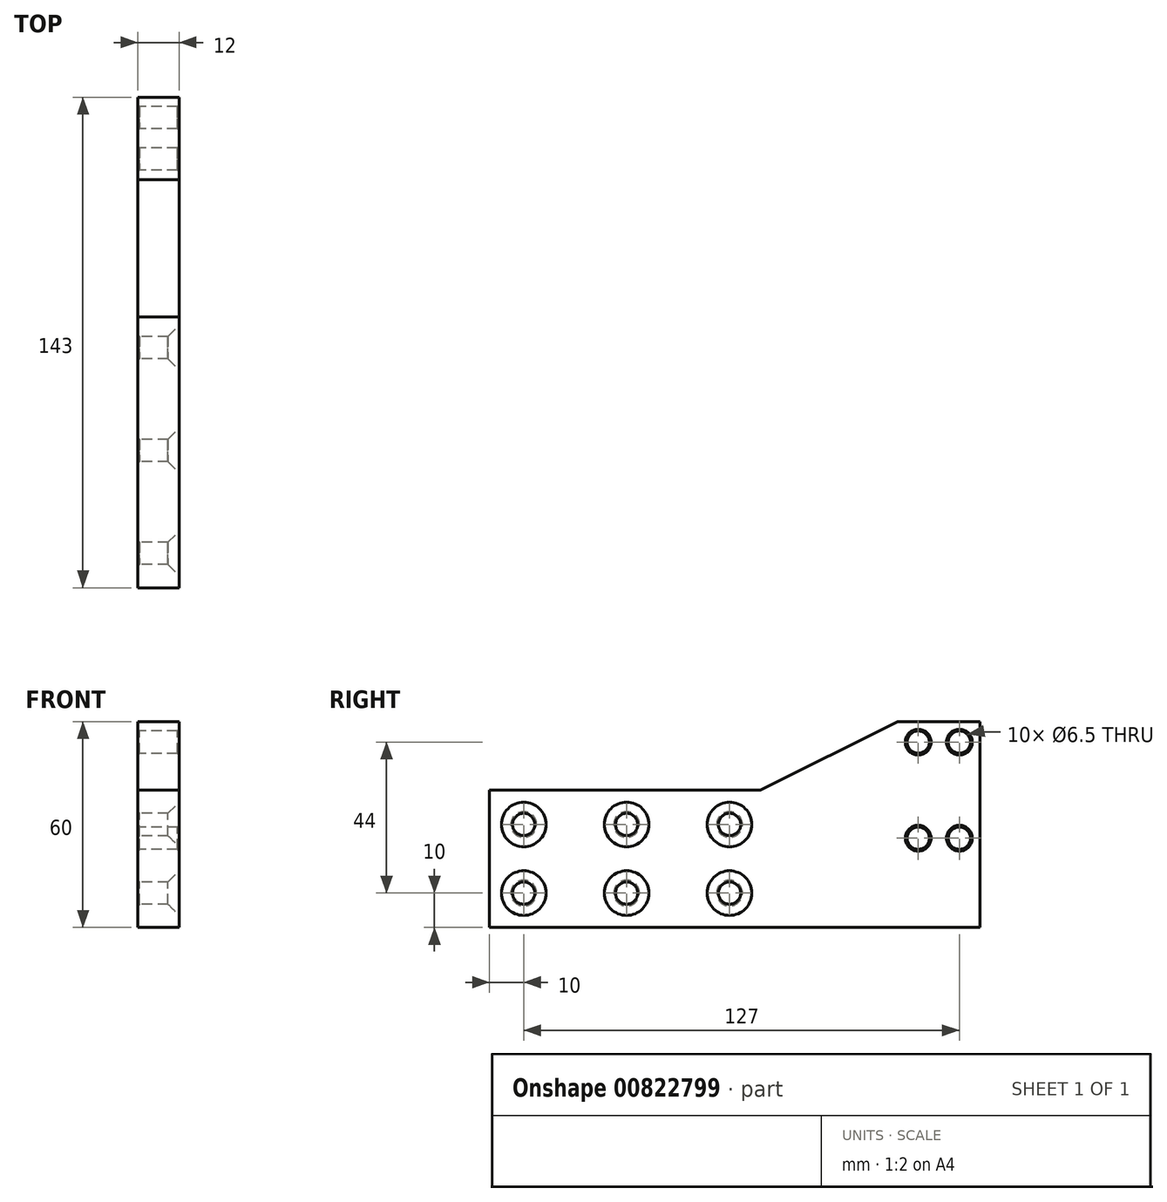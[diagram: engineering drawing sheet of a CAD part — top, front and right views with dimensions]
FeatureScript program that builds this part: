
annotation { "Feature Type Name" : "Feature", "Feature Type Description" : "" }
export const myFeature = defineFeature(function(context is Context, id is Id, definition is map)
    precondition{}
    {
        {
            var Q0;
            Q0=qCreatedBy(makeId("Right.planeOp"),FACE);
            var sketch = newSketch(context, id + "F0", { "sketchPlane" : qUnion([Q0])});
            skLineSegment(sketch, "E0.bottom", {"start": v(-71.5, 20) * mm, "end": v(7.5, 20) * mm});
            skLineSegment(sketch, "E0.top", {"start": v(-71.5, -20) * mm, "end": v(71.5, -20) * mm});
            skLineSegment(sketch, "E0.left", {"start": v(-71.5, 20) * mm, "end": v(-71.5, -20) * mm});
            skLineSegment(sketch, "E0.right", {"start": v(71.5, 20) * mm, "end": v(71.5, -20) * mm});
            skPoint(sketch, "E0.middle", {"position": v(0, 0) * mm});
            skCircle(sketch, "E1", {"center": v(-61.5, 10) * mm, "radius": 3.25 * mm});
            skLineSegment(sketch, "E2", {"start": v(-61.5, 10) * mm, "end": v(-1.5, 10) * mm, "construction": true});
            skCircle(sketch, "E3", {"center": v(-1.5, 10) * mm, "radius": 3.25 * mm});
            skCircle(sketch, "E4", {"center": v(-31.5, 10) * mm, "radius": 3.25 * mm});
            skLineSegment(sketch, "E5", {"start": v(0, 0) * mm, "end": v(-27.42, 0) * mm, "construction": true});
            skCircle(sketch, "E6.MirrorC", {"center": v(-1.5, -10) * mm, "radius": 3.25 * mm});
            skCircle(sketch, "E7.MirrorC", {"center": v(-31.5, -10) * mm, "radius": 3.25 * mm});
            skCircle(sketch, "E8.MirrorC", {"center": v(-61.5, -10) * mm, "radius": 3.25 * mm});
            skLineSegment(sketch, "E9.3", {"start": v(65.5, 34) * mm, "end": v(65.5, 6) * mm, "construction": true});
            skLineSegment(sketch, "E10", {"start": v(47.5, 20) * mm, "end": v(47.5, -20) * mm, "construction": true});
            skCircle(sketch, "E11", {"center": v(65.5, 34) * mm, "radius": 3.25 * mm});
            skCircle(sketch, "E12", {"center": v(53.5, 34) * mm, "radius": 3.25 * mm});
            skCircle(sketch, "E13", {"center": v(53.5, 6) * mm, "radius": 3.25 * mm});
            skCircle(sketch, "E14", {"center": v(65.5, 6) * mm, "radius": 3.25 * mm});
            skLineSegment(sketch, "E15", {"start": v(71.5, 20) * mm, "end": v(71.5, 40) * mm});
            skLineSegment(sketch, "E16", {"start": v(71.5, 40) * mm, "end": v(47.5, 40) * mm});
            skLineSegment(sketch, "E17", {"start": v(47.5, 40) * mm, "end": v(7.5, 20) * mm});
            skLineSegment(sketch, "E18", {"start": v(65.5, 6) * mm, "end": v(53.5, 6) * mm, "construction": true});
            skLineSegment(sketch, "E19", {"start": v(65.5, 34) * mm, "end": v(53.5, 34) * mm, "construction": true});
            skLineSegment(sketch, "E20", {"start": v(53.5, 6) * mm, "end": v(53.5, 34) * mm, "construction": true});
            skSolve(sketch);
        }
        {
            var Q0;
            Q0 = qSketchRegion(id + "F0", true);
            extrude(context, id + "F1", {"entities" : qUnion([Q0]), "depth" : 12 * mm, "offsetDistance" : 25 * mm});
        }
        {
            var Q0;
            Q0=makeQuery(id+"F1.opExtrude","CAP_EDGE",EDGE,{"disambiguationData":[OSD([sQuery(id+"F0.wireOp",EDGE,"E1")])],"isStart":false});
            var Q1;
            Q1=makeQuery(id+"F1.opExtrude","CAP_EDGE",EDGE,{"disambiguationData":[OSD([sQuery(id+"F0.wireOp",EDGE,"E4")])],"isStart":false});
            var Q2;
            Q2=makeQuery(id+"F1.opExtrude","CAP_EDGE",EDGE,{"disambiguationData":[OSD([sQuery(id+"F0.wireOp",EDGE,"E3")])],"isStart":false});
            var Q3;
            Q3=makeQuery(id+"F1.opExtrude","CAP_EDGE",EDGE,{"disambiguationData":[OSD([sQuery(id+"F0.wireOp",EDGE,"E6.MirrorC")])],"isStart":false});
            var Q4;
            Q4=makeQuery(id+"F1.opExtrude","CAP_EDGE",EDGE,{"disambiguationData":[OSD([sQuery(id+"F0.wireOp",EDGE,"E7.MirrorC")])],"isStart":false});
            var Q5;
            Q5=makeQuery(id+"F1.opExtrude","CAP_EDGE",EDGE,{"disambiguationData":[OSD([sQuery(id+"F0.wireOp",EDGE,"E8.MirrorC")])],"isStart":false});
            chamfer(context, id + "F2", {"entities" : qUnion([Q0, Q1, Q2, Q3, Q4, Q5]), "width" : 3.25 * mm, "tangentPropagation" : true});
        }
        {
            var Q0;
            Q0=makeQuery(id+"F1.opExtrude","CAP_EDGE",EDGE,{"disambiguationData":[OSD([sQuery(id+"F0.wireOp",EDGE,"E6.MirrorC")])],"isStart":true});
            var Q1;
            Q1=makeQuery(id+"F1.opExtrude","CAP_EDGE",EDGE,{"disambiguationData":[OSD([sQuery(id+"F0.wireOp",EDGE,"E3")])],"isStart":true});
            var Q2;
            Q2=makeQuery(id+"F1.opExtrude","CAP_EDGE",EDGE,{"disambiguationData":[OSD([sQuery(id+"F0.wireOp",EDGE,"E4")])],"isStart":true});
            var Q3;
            Q3=makeQuery(id+"F1.opExtrude","CAP_EDGE",EDGE,{"disambiguationData":[OSD([sQuery(id+"F0.wireOp",EDGE,"E7.MirrorC")])],"isStart":true});
            var Q4;
            Q4=makeQuery(id+"F1.opExtrude","CAP_EDGE",EDGE,{"disambiguationData":[OSD([sQuery(id+"F0.wireOp",EDGE,"E8.MirrorC")])],"isStart":true});
            var Q5;
            Q5=makeQuery(id+"F1.opExtrude","CAP_EDGE",EDGE,{"disambiguationData":[OSD([sQuery(id+"F0.wireOp",EDGE,"E1")])],"isStart":true});
            var Q6;
            Q6=makeQuery(id+"F1.opExtrude","SWEPT_FACE",FACE,{"disambiguationData":[OSD([sQuery(id+"F0.wireOp",EDGE,"E11")])]});
            var Q7;
            Q7=makeQuery(id+"F1.opExtrude","SWEPT_FACE",FACE,{"disambiguationData":[OSD([sQuery(id+"F0.wireOp",EDGE,"E12")])]});
            var Q8;
            Q8=makeQuery(id+"F1.opExtrude","SWEPT_FACE",FACE,{"disambiguationData":[OSD([sQuery(id+"F0.wireOp",EDGE,"E13")])]});
            var Q9;
            Q9=makeQuery(id+"F1.opExtrude","SWEPT_FACE",FACE,{"disambiguationData":[OSD([sQuery(id+"F0.wireOp",EDGE,"E14")])]});
            chamfer(context, id + "F3", {"entities" : qUnion([Q0, Q1, Q2, Q3, Q4, Q5, Q6, Q7, Q8, Q9]), "width" : 0.5 * mm, "tangentPropagation" : true});
        }
    });
